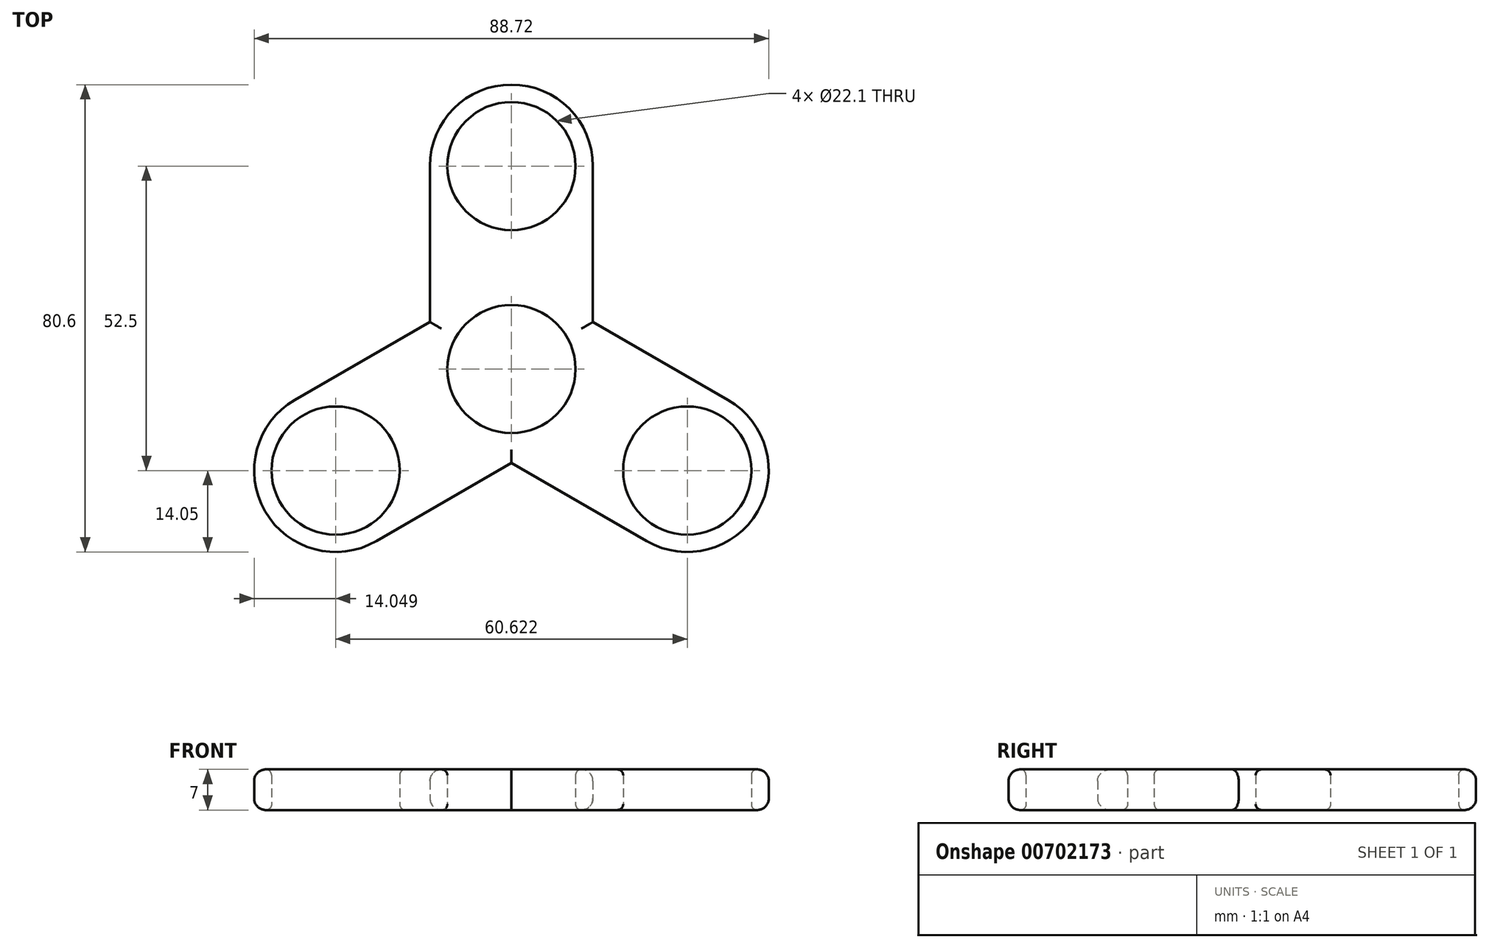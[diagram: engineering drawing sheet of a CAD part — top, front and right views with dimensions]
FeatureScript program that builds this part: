
annotation { "Feature Type Name" : "Feature", "Feature Type Description" : "" }
export const myFeature = defineFeature(function(context is Context, id is Id, definition is map)
    precondition{}
    {
        {
            var Q0;
            Q0=qCreatedBy(makeId("Top.planeOp"),FACE);
            var sketch = newSketch(context, id + "F0", { "sketchPlane" : qUnion([Q0])});
            skCircle(sketch, "E0", {"center": v(0, 0) * mm, "radius": 11.05 * mm});
            skCircle(sketch, "E1", {"center": v(0, 35) * mm, "radius": 11.05 * mm});
            skArc(sketch, "E2.0", {"start": v(-14.05, 0) * mm, "mid": v(0, -14.05) * mm, "end": v(14.05, 0) * mm});
            skArc(sketch, "E3.0", {"start": v(14.05, 35) * mm, "mid": v(0, 49.05) * mm, "end": v(-14.05, 35) * mm});
            skLineSegment(sketch, "E4", {"start": v(-14.05, 35) * mm, "end": v(-14.05, 0) * mm});
            skLineSegment(sketch, "E5", {"start": v(14.05, 0) * mm, "end": v(14.05, 35) * mm});
            skSolve(sketch);
        }
        {
            var Q0;
            Q0=makeQuery(id+"F0.imprint","IMPRINT",FACE,{"disambiguationData":[TD([[makeQuery(id+"F0.imprint","IMPRINT",EDGE,{"derivedFrom":sQuery(id+"F0.wireOp",EDGE,"E0")}),-1.0]])]});
            extrude(context, id + "F1", {"entities" : qUnion([Q0]), "depth" : 7 * mm, "offsetDistance" : 25 * mm});
        }
        {
            var Q0;
            Q0=makeQuery(id+"F1.opExtrude","SWEPT_BODY",BODY,{"disambiguationData":[OSD([sQuery(id+"F0.wireOp",EDGE,"E0"),sQuery(id+"F0.wireOp",EDGE,"E1"),sQuery(id+"F0.wireOp",EDGE,"E2.0"),sQuery(id+"F0.wireOp",EDGE,"E3.0"),sQuery(id+"F0.wireOp",EDGE,"E4"),sQuery(id+"F0.wireOp",EDGE,"E5")])]});
            var Q1;
            Q1=makeQuery(id+"F1.opExtrude","CAP_EDGE",EDGE,{"disambiguationData":[OSD([sQuery(id+"F0.wireOp",EDGE,"E0")])],"isStart":false});
            circularPattern(context, id + "F2", {"operationType" : NewBodyOperationType.ADD, "entities" : qUnion([Q0]), "axis" : qUnion([Q1]), "angle" : 360 * degree, "instanceCount" : 3, "equalSpace" : true});
        }
        {
            var Q0;
            Q0=makeQuery(id+"F2.opPattern","COPY",EDGE,{"derivedFrom":makeQuery(id+"F1.opExtrude","CAP_EDGE",EDGE,{"disambiguationData":[OSD([sQuery(id+"F0.wireOp",EDGE,"E5")])],"isStart":true}),"instanceName":"1"});
            var Q1;
            Q1=makeQuery(id+"F1.opExtrude","CAP_EDGE",EDGE,{"disambiguationData":[OSD([sQuery(id+"F0.wireOp",EDGE,"E4")])],"isStart":true});
            var Q2;
            Q2=makeQuery(id+"F2.opPattern","COPY",EDGE,{"derivedFrom":makeQuery(id+"F1.opExtrude","CAP_EDGE",EDGE,{"disambiguationData":[OSD([sQuery(id+"F0.wireOp",EDGE,"E4")])],"isStart":true}),"instanceName":"2"});
            var Q3;
            Q3=makeQuery(id+"F2.opPattern","COPY",EDGE,{"derivedFrom":makeQuery(id+"F1.opExtrude","CAP_EDGE",EDGE,{"disambiguationData":[OSD([sQuery(id+"F0.wireOp",EDGE,"E5")])],"isStart":false}),"instanceName":"1"});
            var Q4;
            Q4=makeQuery(id+"F1.opExtrude","CAP_EDGE",EDGE,{"disambiguationData":[OSD([sQuery(id+"F0.wireOp",EDGE,"E4")])],"isStart":false});
            var Q5;
            Q5=makeQuery(id+"F2.opPattern","COPY",EDGE,{"derivedFrom":makeQuery(id+"F1.opExtrude","CAP_EDGE",EDGE,{"disambiguationData":[OSD([sQuery(id+"F0.wireOp",EDGE,"E5")])],"isStart":false}),"instanceName":"2"});
            fillet(context, id + "F3", {"entities" : qUnion([Q0, Q1, Q2, Q3, Q4, Q5]), "radius" : 2 * mm, "tangentPropagation" : true, "allowEdgeOverflow" : false});
        }
        {
            var Q0;
            Q0=makeQuery(id+"F2.opPattern","COPY",EDGE,{"derivedFrom":makeQuery(id+"F1.opExtrude","CAP_EDGE",EDGE,{"disambiguationData":[OSD([sQuery(id+"F0.wireOp",EDGE,"E1")])],"isStart":true}),"instanceName":"1"});
            var Q1;
            Q1=makeQuery(id+"F2.opPattern","COPY",EDGE,{"derivedFrom":makeQuery(id+"F1.opExtrude","CAP_EDGE",EDGE,{"disambiguationData":[OSD([sQuery(id+"F0.wireOp",EDGE,"E1")])],"isStart":false}),"instanceName":"1"});
            var Q2;
            Q2=makeQuery(id+"F1.opExtrude","CAP_EDGE",EDGE,{"disambiguationData":[OSD([sQuery(id+"F0.wireOp",EDGE,"E0")])],"isStart":true});
            var Q3;
            Q3=makeQuery(id+"F1.opExtrude","CAP_EDGE",EDGE,{"disambiguationData":[OSD([sQuery(id+"F0.wireOp",EDGE,"E0")])],"isStart":false});
            var Q4;
            Q4=makeQuery(id+"F1.opExtrude","CAP_EDGE",EDGE,{"disambiguationData":[OSD([sQuery(id+"F0.wireOp",EDGE,"E1")])],"isStart":true});
            var Q5;
            Q5=makeQuery(id+"F1.opExtrude","CAP_EDGE",EDGE,{"disambiguationData":[OSD([sQuery(id+"F0.wireOp",EDGE,"E1")])],"isStart":false});
            var Q6;
            Q6=makeQuery(id+"F2.opPattern","COPY",EDGE,{"derivedFrom":makeQuery(id+"F1.opExtrude","CAP_EDGE",EDGE,{"disambiguationData":[OSD([sQuery(id+"F0.wireOp",EDGE,"E1")])],"isStart":true}),"instanceName":"2"});
            var Q7;
            Q7=makeQuery(id+"F2.opPattern","COPY",EDGE,{"derivedFrom":makeQuery(id+"F1.opExtrude","CAP_EDGE",EDGE,{"disambiguationData":[OSD([sQuery(id+"F0.wireOp",EDGE,"E1")])],"isStart":false}),"instanceName":"2"});
            fillet(context, id + "F4", {"entities" : qUnion([Q0, Q1, Q2, Q3, Q4, Q5, Q6, Q7]), "radius" : 1 * mm, "tangentPropagation" : true, "allowEdgeOverflow" : false});
        }
    });
